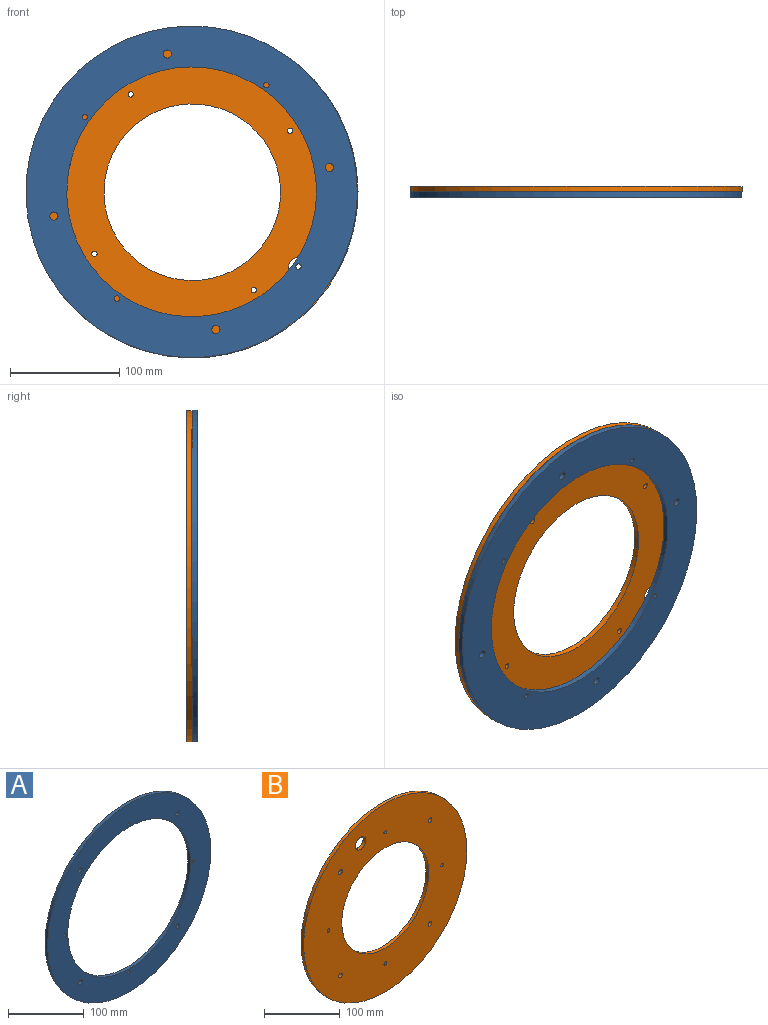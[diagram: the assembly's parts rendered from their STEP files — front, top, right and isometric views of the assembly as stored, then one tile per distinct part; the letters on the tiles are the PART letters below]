
ASSEMBLY  parts=2 mates=1
PART A: 12 faces, bbox 304x5x304 mm
  f0: cylinder r=114.5mm len=229mm, axis (0,1,0), area 3597.1mm2, adj f10,f11
  f1: cylinder r=2.5mm len=5mm, axis (0,1,0), area 78.5mm2, adj f10,f11
  f2: cylinder r=2.5mm len=5mm, axis (0,1,0), area 78.5mm2, adj f10,f11
  f3: cylinder r=2.5mm len=5mm, axis (0,1,0), area 78.5mm2, adj f10,f11
  f4: cylinder r=2.5mm len=5mm, axis (0,1,0), area 78.5mm2, adj f10,f11
  f5: cylinder r=3.75mm len=7.5mm, axis (0,1,0), area 117.8mm2, adj f10,f11
  f6: cylinder r=3.75mm len=7.5mm, axis (0,1,0), area 117.8mm2, adj f10,f11
  f7: cylinder r=3.75mm len=7.5mm, axis (0,1,0), area 117.8mm2, adj f10,f11
  f8: cylinder r=3.75mm len=7.5mm, axis (0,1,0), area 117.8mm2, adj f10,f11
  f9: cylinder r=152mm len=304mm, axis (0,1,0), area 4775.2mm2, adj f10,f11
  f10: plane 304x304mm, normal (0,-1,0), area 31141mm2, adj f0,f1,f2,f3,f4,f5,f6,f7
  f11: plane 304x304mm, normal (0,1,0), area 31141mm2, adj f0,f1,f2,f3,f4,f5,f6,f7
PART B: 13 faces, bbox 304x5x304 mm
  f0: cylinder r=81mm len=162mm, axis (0,1,0), area 2544.7mm2, adj f2,f3
  f1: cylinder r=152mm len=304mm, axis (0,1,0), area 4775.2mm2, adj f2,f3
  f2: plane 304x304mm, normal (0,-1,0), area 51440.2mm2, adj f0,f1,f4,f5,f6,f7,f8,f9
  f3: plane 304x304mm, normal (0,1,0), area 51440.2mm2, adj f0,f1,f4,f5,f6,f7,f8,f9
  f4: cylinder r=2.5mm len=5mm, axis (0,-1,0), area 78.5mm2, adj f2,f3
  f5: cylinder r=2.5mm len=5mm, axis (0,-1,0), area 78.5mm2, adj f2,f3
  f6: cylinder r=2.5mm len=5mm, axis (0,-1,0), area 78.5mm2, adj f2,f3
  f7: cylinder r=2.5mm len=5mm, axis (0,-1,0), area 78.5mm2, adj f2,f3
  f8: cylinder r=3.5mm len=7mm, axis (0,-1,0), area 110mm2, adj f2,f3
  f9: cylinder r=3.5mm len=7mm, axis (0,-1,0), area 110mm2, adj f2,f3
  f10: cylinder r=3.5mm len=7mm, axis (0,-1,0), area 110mm2, adj f2,f3
  f11: cylinder r=9.75mm len=19.5mm, axis (0,-1,0), area 306.3mm2, adj f2,f3
  f12: cylinder r=3.5mm len=7mm, axis (0,-1,0), area 110mm2, adj f2,f3
PLACE A rot(axis=(0,-1,0),55deg) t=(-0.57,0,0.4)mm
PLACE B rot(axis=(0,1,0),147.9deg) t=(0,0,0)mm
MATE revolute B.f2 <-> A.f0  axis (0,-1,0) through (-0.57,-5,0.4)mm
